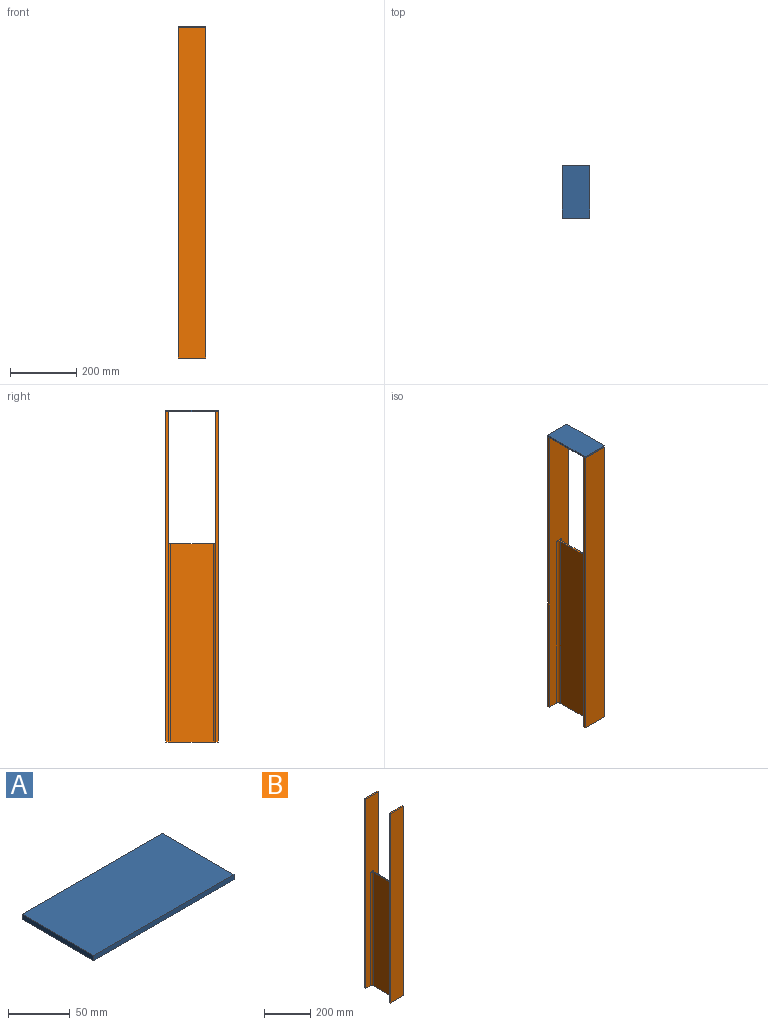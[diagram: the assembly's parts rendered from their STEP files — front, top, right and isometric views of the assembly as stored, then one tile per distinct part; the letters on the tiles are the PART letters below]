
ASSEMBLY  parts=2 mates=1
PART A: 6 faces, bbox 160x82x5 mm
  f0: plane 82x5mm, normal (1,0,0), area 410mm2, adj f1,f3,f4,f5
  f1: plane 160x5mm, normal (0,1,0), area 800mm2, adj f0,f2,f4,f5
  f2: plane 82x5mm, normal (-1,0,0), area 410mm2, adj f1,f3,f4,f5
  f3: plane 160x5mm, normal (0,-1,0), area 800mm2, adj f0,f2,f4,f5
  f4: plane 160x82mm, normal (0,0,1), area 13120mm2, adj f0,f1,f2,f3
  f5: plane 160x82mm, normal (0,0,-1), area 13120mm2, adj f0,f1,f2,f3
PART B: 18 faces, bbox 82x160x1000 mm
  f0: cylinder r=9mm len=600mm, axis (0,0,-1), area 8482.3mm2, adj f1,f13,f16,f17
  f1: plane 600x127.2mm, normal (-1,0,0), area 76320mm2, adj f0,f2,f16,f17
  f2: cylinder r=9mm len=600mm, axis (0,0,-1), area 8482.3mm2, adj f1,f12,f16,f17
  f3: cylinder r=9mm len=600mm, axis (0,0,-1), area 8482.3mm2, adj f4,f12,f16,f17
  f4: plane 600x127.2mm, normal (1,0,0), area 76320mm2, adj f3,f5,f16,f17
  f5: cylinder r=9mm len=600mm, axis (0,0,-1), area 8482.3mm2, adj f4,f13,f16,f17
  f6: plane 82x7.4mm, normal (0,0,1), area 606.8mm2, adj f7,f8,f13,f14
  f7: plane 1000x82mm, normal (0,1,0), area 82000mm2, adj f6,f8,f14,f16
  f8: plane 1000x7.4mm, normal (-1,0,0), area 7400mm2, adj f6,f7,f13,f16
  f9: plane 1000x7.4mm, normal (-1,0,0), area 7400mm2, adj f10,f12,f15,f16
  f10: plane 1000x82mm, normal (0,-1,0), area 82000mm2, adj f9,f11,f15,f16
  f11: plane 1000x7.4mm, normal (1,0,0), area 7400mm2, adj f10,f12,f15,f16
  f12: plane 1000x82mm, normal (0,1,0), area 68200mm2, adj f2,f3,f9,f11,f15,f16,f17
  f13: plane 1000x82mm, normal (0,-1,0), area 68200mm2, adj f0,f5,f6,f8,f14,f16,f17
  f14: plane 1000x7.4mm, normal (1,0,0), area 7400mm2, adj f6,f7,f13,f16
  f15: plane 82x7.4mm, normal (0,0,1), area 606.8mm2, adj f9,f10,f11,f12
  f16: plane 160x82mm, normal (0,0,-1), area 2009.1mm2, adj f0,f1,f2,f3,f4,f5,f7,f8
  f17: plane 145.2x23mm, normal (0,0,1), area 795.5mm2, adj f0,f1,f2,f3,f4,f5,f12,f13
PLACE A rot(axis=(0,0,-1),90deg) t=(-480.53,-52.85,836.88)mm
PLACE B t=(-480.53,-52.85,-163.12)mm
MATE fastened A.f5 <-> B.f6  axis (0,0,-1) through (-521.53,27.15,836.88)mm
